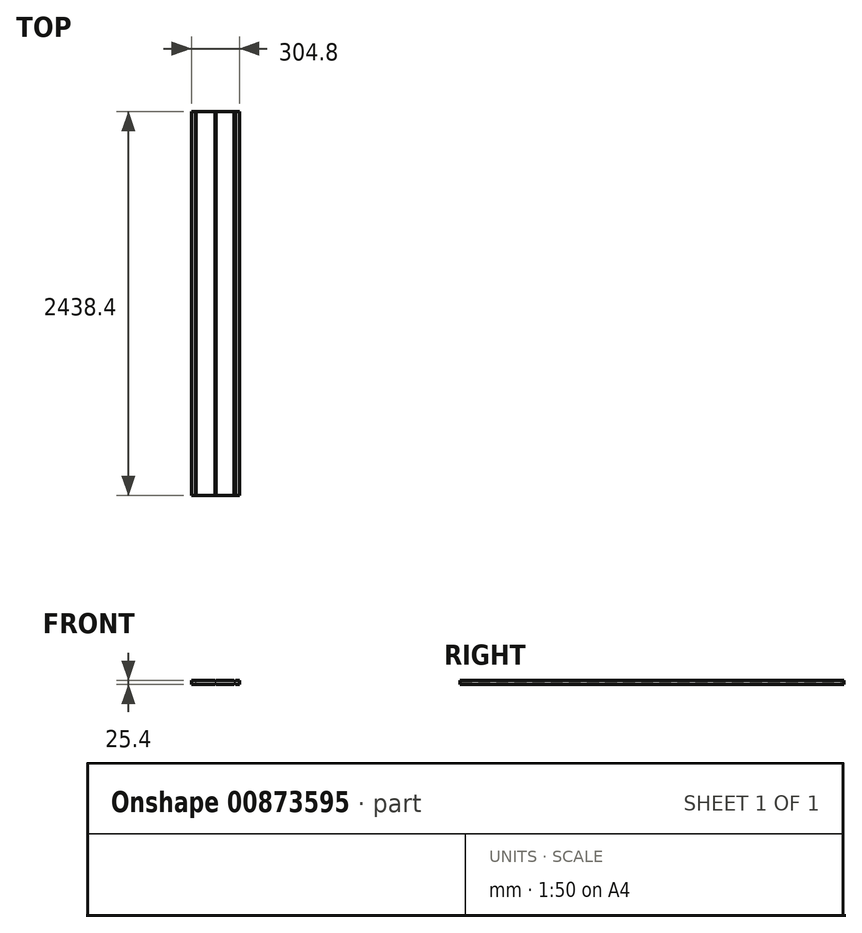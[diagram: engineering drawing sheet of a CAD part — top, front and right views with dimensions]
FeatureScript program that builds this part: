
annotation { "Feature Type Name" : "Feature", "Feature Type Description" : "" }
export const myFeature = defineFeature(function(context is Context, id is Id, definition is map)
    precondition{}
    {
        {
            var Q0;
            Q0=qCreatedBy(makeId("Front.planeOp"),FACE);
            var sketch = newSketch(context, id + "F0", { "sketchPlane" : qUnion([Q0])});
            skLineSegment(sketch, "E0.bottom", {"start": v(0, 0) * mm, "end": v(25.4, 0) * mm});
            skLineSegment(sketch, "E0.top", {"start": v(0, 25.4) * mm, "end": v(25.4, 25.4) * mm});
            skLineSegment(sketch, "E0.left", {"start": v(0, 0) * mm, "end": v(0, 25.4) * mm});
            skLineSegment(sketch, "E0.right", {"start": v(304.8, 0) * mm, "end": v(304.8, 25.4) * mm});
            skLineSegment(sketch, "E1", {"start": v(25.4, 25.4) * mm, "end": v(25.4, 19.05) * mm});
            skLineSegment(sketch, "E2", {"start": v(279.4, 25.4) * mm, "end": v(279.4, 19.05) * mm});
            skLineSegment(sketch, "E3.0", {"start": v(31.75, 25.4) * mm, "end": v(31.75, 19.05) * mm});
            skLineSegment(sketch, "E4.0", {"start": v(149.22, 25.4) * mm, "end": v(149.22, 19.05) * mm});
            skLineSegment(sketch, "E5.0", {"start": v(155.58, 25.4) * mm, "end": v(155.58, 19.05) * mm});
            skLineSegment(sketch, "E6.0", {"start": v(273.05, 25.4) * mm, "end": v(273.05, 19.05) * mm});
            skLineSegment(sketch, "E7", {"start": v(25.4, 19.05) * mm, "end": v(31.75, 19.05) * mm});
            skLineSegment(sketch, "E8", {"start": v(25.4, 6.35) * mm, "end": v(31.75, 6.35) * mm});
            skLineSegment(sketch, "E9.trimOffspring", {"start": v(149.22, 19.05) * mm, "end": v(155.58, 19.05) * mm});
            skPoint(sketch, "E10.orphan", {"position": v(152.4, 25.4) * mm});
            skLineSegment(sketch, "E11.trimOffspring", {"start": v(25.4, 6.35) * mm, "end": v(25.4, 0) * mm});
            skLineSegment(sketch, "E12.trimOffspring", {"start": v(31.75, 6.35) * mm, "end": v(31.75, 0) * mm});
            skLineSegment(sketch, "E13.trimOffspring", {"start": v(149.22, 6.35) * mm, "end": v(155.58, 6.35) * mm});
            skLineSegment(sketch, "E14.trimOffspring", {"start": v(149.22, 6.35) * mm, "end": v(149.22, 0) * mm});
            skLineSegment(sketch, "E15.trimOffspring", {"start": v(155.58, 6.35) * mm, "end": v(155.58, 0) * mm});
            skLineSegment(sketch, "E16.trimOffspring", {"start": v(273.05, 19.05) * mm, "end": v(279.4, 19.05) * mm});
            skLineSegment(sketch, "E17.trimOffspring", {"start": v(273.05, 6.35) * mm, "end": v(279.4, 6.35) * mm});
            skLineSegment(sketch, "E18.trimOffspring", {"start": v(279.4, 6.35) * mm, "end": v(279.4, 0) * mm});
            skLineSegment(sketch, "E19.trimOffspring", {"start": v(273.05, 6.35) * mm, "end": v(273.05, 0) * mm});
            skLineSegment(sketch, "E20.trimOffspring", {"start": v(279.4, 0) * mm, "end": v(304.8, 0) * mm});
            skLineSegment(sketch, "E21.trimOffspring", {"start": v(279.4, 25.4) * mm, "end": v(304.8, 25.4) * mm});
            skLineSegment(sketch, "E22.trimOffspring", {"start": v(155.58, 25.4) * mm, "end": v(273.05, 25.4) * mm});
            skLineSegment(sketch, "E23.trimOffspring", {"start": v(155.58, 0) * mm, "end": v(273.05, 0) * mm});
            skLineSegment(sketch, "E24.trimOffspring", {"start": v(31.75, 0) * mm, "end": v(149.22, 0) * mm});
            skLineSegment(sketch, "E25.trimOffspring", {"start": v(31.75, 25.4) * mm, "end": v(149.22, 25.4) * mm});
            skSolve(sketch);
        }
        {
            var Q0;
            Q0 = qSketchRegion(id + "F0", true);
            extrude(context, id + "F1", {"entities" : qUnion([Q0]), "depth" : 2438.4 * mm, "offsetDistance" : 25.4 * mm});
        }
    });
